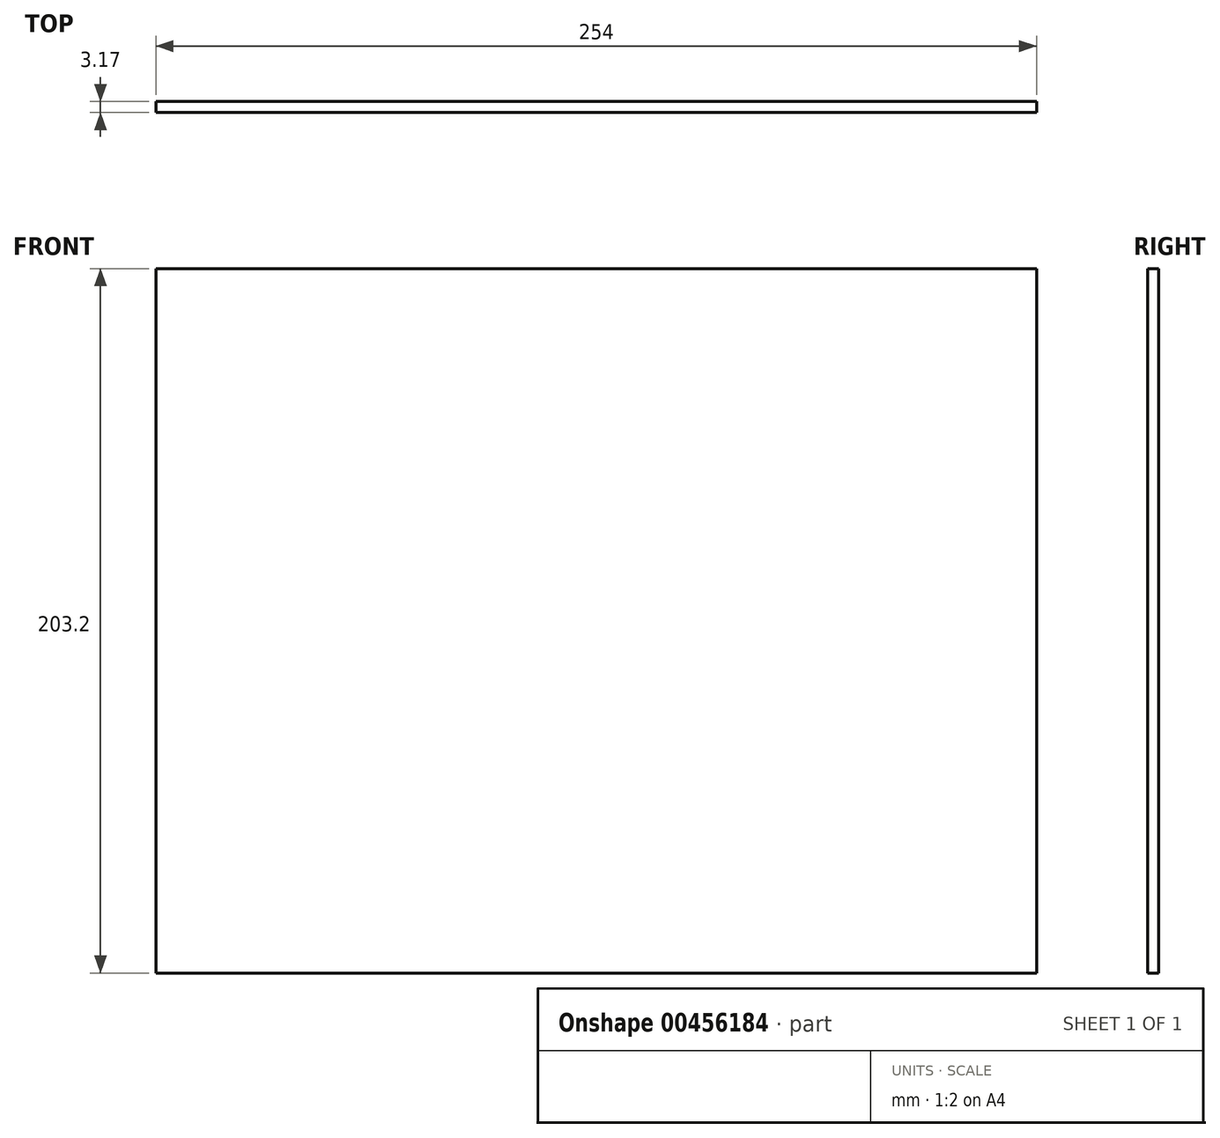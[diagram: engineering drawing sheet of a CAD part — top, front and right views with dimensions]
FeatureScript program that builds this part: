
annotation { "Feature Type Name" : "Feature", "Feature Type Description" : "" }
export const myFeature = defineFeature(function(context is Context, id is Id, definition is map)
    precondition{}
    {
        {
            var Q0;
            Q0=qCreatedBy(makeId("Front.planeOp"),FACE);
            var sketch = newSketch(context, id + "F0", { "sketchPlane" : qUnion([Q0])});
            skLineSegment(sketch, "E0.bottom", {"start": v(-127, 101.6) * mm, "end": v(127, 101.6) * mm});
            skLineSegment(sketch, "E0.top", {"start": v(-127, -101.6) * mm, "end": v(127, -101.6) * mm});
            skLineSegment(sketch, "E0.left", {"start": v(-127, 101.6) * mm, "end": v(-127, -101.6) * mm});
            skLineSegment(sketch, "E0.right", {"start": v(127, 101.6) * mm, "end": v(127, -101.6) * mm});
            skPoint(sketch, "E1", {"position": v(0, 0) * mm});
            skPoint(sketch, "E1.positionSnap0", {"position": v(127, 0) * mm});
            skPoint(sketch, "E1.positionSnap1", {"position": v(0, 101.6) * mm});
            skSolve(sketch);
        }
        {
            var Q0;
            Q0=makeQuery(id+"F0.imprint","IMPRINT",FACE,{"disambiguationData":[TD([[makeQuery(id+"F0.imprint","IMPRINT",EDGE,{"derivedFrom":sQuery(id+"F0.wireOp",EDGE,"E0.bottom")}),-1.0]])]});
            extrude(context, id + "F1", {"entities" : qUnion([Q0]), "depth" : 3.17 * mm});
        }
    });
